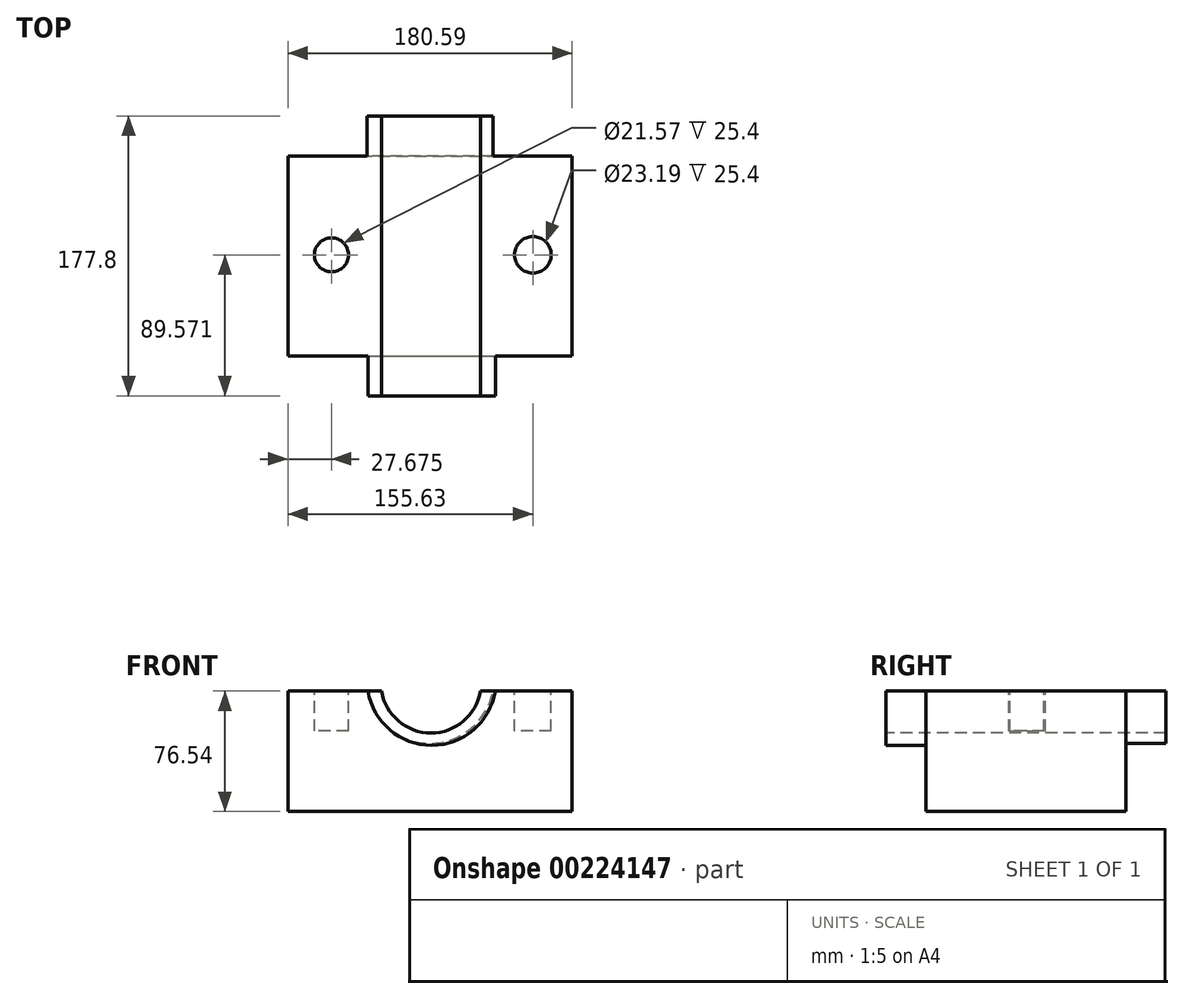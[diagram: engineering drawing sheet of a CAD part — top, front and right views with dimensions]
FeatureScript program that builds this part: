
annotation { "Feature Type Name" : "Feature", "Feature Type Description" : "" }
export const myFeature = defineFeature(function(context is Context, id is Id, definition is map)
    precondition{}
    {
        {
            var Q0;
            Q0=qCreatedBy(makeId("Front.planeOp"),FACE);
            var sketch = newSketch(context, id + "F0", { "sketchPlane" : qUnion([Q0])});
            skLineSegment(sketch, "E0.bottom", {"start": v(-91.35, 32.22) * mm, "end": v(89.24, 32.22) * mm});
            skLineSegment(sketch, "E0.top", {"start": v(-91.35, -44.32) * mm, "end": v(89.24, -44.32) * mm});
            skLineSegment(sketch, "E0.left", {"start": v(-91.35, 32.22) * mm, "end": v(-91.35, -44.32) * mm});
            skLineSegment(sketch, "E0.right", {"start": v(89.24, 32.22) * mm, "end": v(89.24, -44.32) * mm});
            skSolve(sketch);
        }
        {
            var Q0;
            Q0=makeQuery(id+"F0.imprint","IMPRINT",FACE,{"disambiguationData":[TD([[makeQuery(id+"F0.imprint","IMPRINT",EDGE,{"derivedFrom":sQuery(id+"F0.wireOp",EDGE,"E0.bottom")}),-1.0]])]});
            extrude(context, id + "F1", {"entities" : qUnion([Q0]), "depth" : 127 * mm});
        }
        {
            var Q0;
            Q0=makeQuery(id+"F1.opExtrude","CAP_FACE",FACE,{"disambiguationData":[OSD([sQuery(id+"F0.wireOp",EDGE,"E0.bottom"),sQuery(id+"F0.wireOp",EDGE,"E0.top"),sQuery(id+"F0.wireOp",EDGE,"E0.left"),sQuery(id+"F0.wireOp",EDGE,"E0.right")])],"isStart":false});
            var sketch = newSketch(context, id + "F2", { "sketchPlane" : qUnion([Q0])});
            skArc(sketch, "E1", {"start": v(-40.38, 32.22) * mm, "mid": v(0, -2.23) * mm, "end": v(40.38, 32.22) * mm});
            skArc(sketch, "E2", {"start": v(-31.91, 32.22) * mm, "mid": v(-0.45, 5.58) * mm, "end": v(31, 32.22) * mm});
            skSolve(sketch);
        }
        {
            var Q0;
            {var subQ0=sQuery(id+"F2.wireOp",EDGE,"E1");Q0=makeQuery(id+"F2.imprint","IMPRINT",FACE,{"disambiguationData":[TD([[makeQuery(id+"F2.imprint","IMPRINT",EDGE,{"derivedFrom":subQ0}),1.0]])]});}
            var sketch = newSketch(context, id + "F3", { "sketchPlane" : qUnion([Q0])});
            skSolve(sketch);
        }
        {
            var Q0;
            {var subQ0=sQuery(id+"F2.wireOp",EDGE,"E2");Q0=makeQuery(id+"F2.imprint","IMPRINT",FACE,{"disambiguationData":[TD([[makeQuery(id+"F2.imprint","IMPRINT",EDGE,{"derivedFrom":subQ0}),1.0]])]});}
            extrude(context, id + "F4", {"entities" : qUnion([Q0]), "operationType" : NewBodyOperationType.REMOVE, "endBound" : BoundingType.THROUGH_ALL, "oppositeDirection" : true, "depth" : 25.4 * mm});
        }
        {
            var Q0;
            {var subQ0=sQuery(id+"F2.wireOp",EDGE,"E1");Q0=makeQuery(id+"F3.imprint","IMPRINT",FACE,{"disambiguationData":[TD([[makeQuery(id+"F3.imprint","IMPRINT",EDGE,{"derivedFrom":makeQuery(id+"F2.imprint","IMPRINT",EDGE,{"derivedFrom":subQ0})}),1.0]])]});}
            var sketch = newSketch(context, id + "F5", { "sketchPlane" : qUnion([Q0])});
            skSolve(sketch);
        }
        {
            var Q0;
            Q0 = qSketchRegion(id + "F5", true);
            var Q1;
            {var subQ0=sQuery(id+"F2.wireOp",EDGE,"E1");Q1=makeQuery(id+"F3.imprint","IMPRINT",FACE,{"disambiguationData":[TD([[makeQuery(id+"F3.imprint","IMPRINT",EDGE,{"derivedFrom":makeQuery(id+"F2.imprint","IMPRINT",EDGE,{"derivedFrom":subQ0})}),1.0]])]});}
            extrude(context, id + "F6", {"entities" : qUnion([Q0, Q1]), "operationType" : NewBodyOperationType.ADD, "depth" : 25.4 * mm});
        }
        {
            var Q0;
            Q0=makeQuery(id+"F1.opExtrude","CAP_FACE",FACE,{"disambiguationData":[OSD([sQuery(id+"F0.wireOp",EDGE,"E0.bottom"),sQuery(id+"F0.wireOp",EDGE,"E0.top"),sQuery(id+"F0.wireOp",EDGE,"E0.left"),sQuery(id+"F0.wireOp",EDGE,"E0.right")])],"isStart":true});
            var sketch = newSketch(context, id + "F7", { "sketchPlane" : qUnion([Q0])});
            skArc(sketch, "E3", {"start": v(-38.87, 32.22) * mm, "mid": v(1.06, -1.03) * mm, "end": v(40.99, 32.22) * mm});
            skSolve(sketch);
        }
        {
            var Q0;
            Q0 = qSketchRegion(id + "F7", true);
            var Q1;
            {var subQ0=sQuery(id+"F7.wireOp",EDGE,"E3");Q1=makeQuery(id+"F7.imprint","IMPRINT",FACE,{"disambiguationData":[TD([[makeQuery(id+"F7.imprint","IMPRINT",EDGE,{"derivedFrom":subQ0}),1.0]])]});}
            extrude(context, id + "F8", {"entities" : qUnion([Q0, Q1]), "operationType" : NewBodyOperationType.ADD, "depth" : 25.4 * mm});
        }
        {
            var Q0;
            {var subQ0=sQuery(id+"F0.wireOp",EDGE,"E0.bottom");var subQ1=makeQuery(id+"F1.opExtrude","SWEPT_FACE",FACE,{"disambiguationData":[OSD([subQ0])]});var subQ3=sQuery(id+"F0.wireOp",EDGE,"E0.left");var subQ8=makeQuery(id+"F1.opExtrude","SWEPT_FACE",FACE,{"disambiguationData":[OSD([subQ3])]});var subQ9=makeQuery(id+"F4.boolean.opBoolean","SPLIT",EDGE,{"disambiguationData":[TD([subQ8])],"derivedFrom":makeQuery(id+"F1.opExtrude","CAP_EDGE",EDGE,{"disambiguationData":[OSD([subQ0])],"isStart":true})});var subQ10=makeQuery(id+"F1.opExtrude","CAP_EDGE",EDGE,{"disambiguationData":[OSD([subQ0])],"isStart":false});Q0=makeQuery(id+"F8.boolean.opBoolean","MERGE",FACE,{"derivedFrom":[makeQuery(id+"F6.boolean.opBoolean","MERGE",FACE,{"derivedFrom":[makeQuery(id+"F4.boolean.opBoolean","SPLIT",FACE,{"disambiguationData":[TD([subQ8])],"derivedFrom":subQ1}),makeQuery(id+"F6.opExtrude","SWEPT_FACE",FACE,{"disambiguationData":[OSD([subQ0]),TDD([makeQuery(id+"F3.imprint","IMPRINT",EDGE,{"derivedFrom":makeQuery(id+"F2.imprint","IMPRINT",EDGE,{"disambiguationData":[TD([[makeQuery(id+"F2.imprint","INTERSECT",VERTEX,{"disambiguationData":[OD(0.0)],"derivedFrom":[subQ10,sQuery(id+"F2.wireOp",EDGE,"E1")]}),-1.0]])],"derivedFrom":subQ10})})])]})]}),makeQuery(id+"F8.opExtrude","SWEPT_FACE",FACE,{"disambiguationData":[OSD([subQ0]),TDD([makeQuery(id+"F7.imprint","IMPRINT",EDGE,{"disambiguationData":[TD([[makeQuery(id+"F7.imprint","INTERSECT",VERTEX,{"derivedFrom":[subQ9,sQuery(id+"F7.wireOp",EDGE,"E3")]}),-1.0]])],"derivedFrom":subQ9})])]})]});}
            var sketch = newSketch(context, id + "F9", { "sketchPlane" : qUnion([Q0])});
            skCircle(sketch, "E4", {"center": v(-63.68, -62.83) * mm, "radius": 10.79 * mm});
            skCircle(sketch, "E5", {"center": v(64.28, -62.83) * mm, "radius": 11.6 * mm});
            skSolve(sketch);
        }
        {
            var Q0;
            Q0=makeQuery(id+"F9.imprint","IMPRINT",FACE,{"disambiguationData":[TD([[makeQuery(id+"F9.imprint","IMPRINT",EDGE,{"derivedFrom":sQuery(id+"F9.wireOp",EDGE,"E4")}),1.0]])]});
            var Q1;
            Q1=makeQuery(id+"F9.imprint","IMPRINT",FACE,{"disambiguationData":[TD([[makeQuery(id+"F9.imprint","IMPRINT",EDGE,{"derivedFrom":sQuery(id+"F9.wireOp",EDGE,"E5")}),1.0]])]});
            extrude(context, id + "F10", {"entities" : qUnion([Q0, Q1]), "operationType" : NewBodyOperationType.REMOVE, "oppositeDirection" : true, "depth" : 25.4 * mm});
        }
    });
